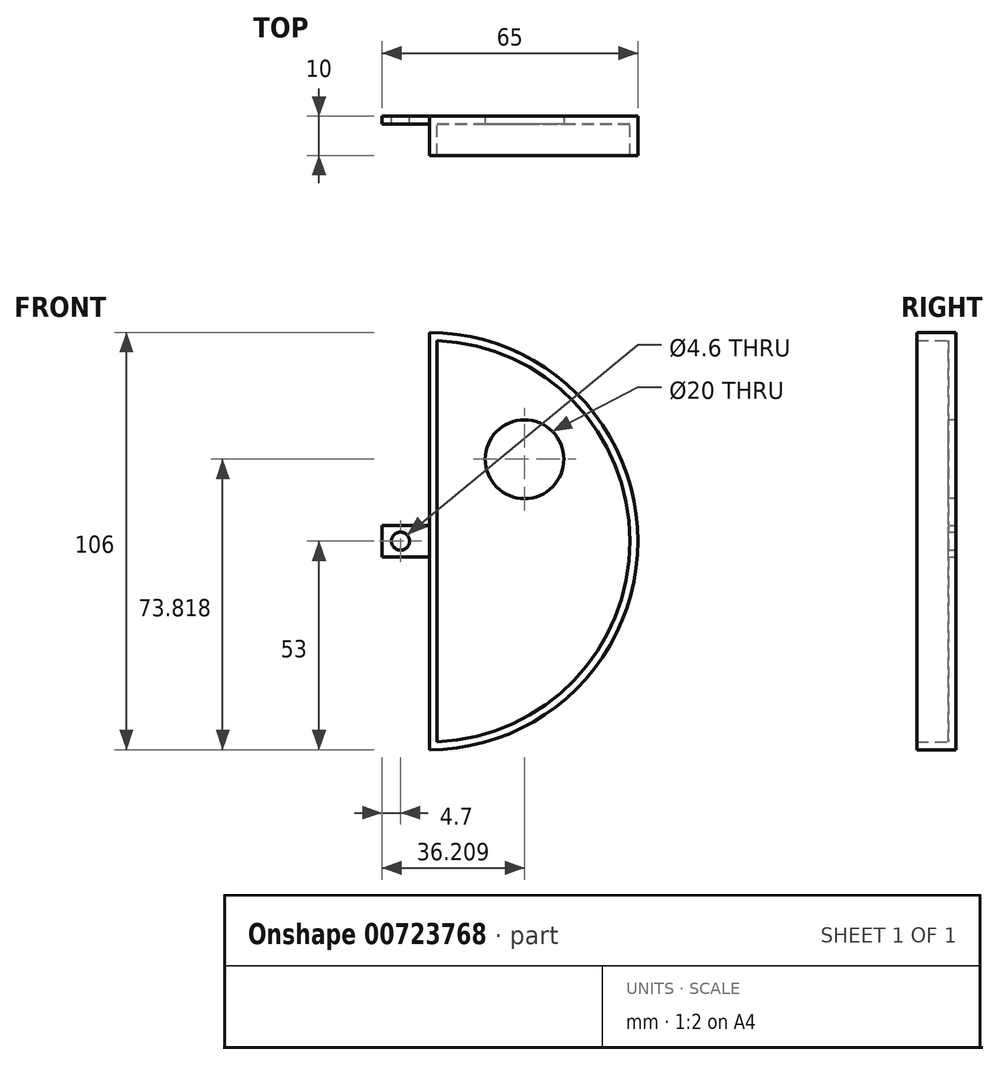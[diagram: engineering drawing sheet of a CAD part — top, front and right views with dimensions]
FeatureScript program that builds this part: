
annotation { "Feature Type Name" : "Feature", "Feature Type Description" : "" }
export const myFeature = defineFeature(function(context is Context, id is Id, definition is map)
    precondition{}
    {
        {
            var Q0;
            Q0=qCreatedBy(makeId("Front.planeOp"),FACE);
            var sketch = newSketch(context, id + "F0", { "sketchPlane" : qUnion([Q0])});
            skArc(sketch, "E0", {"start": v(0, -53) * mm, "mid": v(53, 0) * mm, "end": v(0, 53) * mm});
            skLineSegment(sketch, "E1", {"start": v(0, 53) * mm, "end": v(0, -53) * mm});
            skSolve(sketch);
        }
        {
            var Q0;
            Q0 = qSketchRegion(id + "F0", true);
            extrude(context, id + "F1", {"entities" : qUnion([Q0]), "depth" : 10 * mm, "offsetDistance" : 25 * mm});
        }
        {
            var Q0;
            Q0=makeQuery(id+"F1.opExtrude","CAP_FACE",FACE,{"disambiguationData":[OSD([sQuery(id+"F0.wireOp",EDGE,"E0"),sQuery(id+"F0.wireOp",EDGE,"E1")])],"isStart":false});
            shell(context, id + "F2", {"entities" : qUnion([Q0]), "thickness" : 2 * mm});
        }
        {
            var Q0;
            Q0=qCreatedBy(makeId("Front.planeOp"),FACE);
            var sketch = newSketch(context, id + "F3", { "sketchPlane" : qUnion([Q0])});
            skLineSegment(sketch, "E2.bottom", {"start": v(0, -4) * mm, "end": v(-12, -4) * mm});
            skLineSegment(sketch, "E2.top", {"start": v(0, 4) * mm, "end": v(-12, 4) * mm});
            skLineSegment(sketch, "E2.left", {"start": v(0, -4) * mm, "end": v(0, 4) * mm});
            skLineSegment(sketch, "E2.right", {"start": v(-12, -4) * mm, "end": v(-12, 4) * mm});
            skSolve(sketch);
        }
        {
            var Q0;
            Q0 = qSketchRegion(id + "F3", true);
            extrude(context, id + "F4", {"entities" : qUnion([Q0]), "operationType" : NewBodyOperationType.ADD, "depth" : 2 * mm, "offsetDistance" : 25 * mm});
        }
        {
            var Q0;
            Q0=makeQuery(id+"F4.boolean.opBoolean","MERGE",FACE,{"derivedFrom":[makeQuery(id+"F1.opExtrude","CAP_FACE",FACE,{"disambiguationData":[OSD([sQuery(id+"F0.wireOp",EDGE,"E0"),sQuery(id+"F0.wireOp",EDGE,"E1")])],"isStart":true}),makeQuery(id+"F4.opExtrude","CAP_FACE",FACE,{"disambiguationData":[OSD([sQuery(id+"F3.wireOp",EDGE,"E2.bottom"),sQuery(id+"F3.wireOp",EDGE,"E2.top"),sQuery(id+"F3.wireOp",EDGE,"E2.left"),sQuery(id+"F3.wireOp",EDGE,"E2.right")])],"isStart":true})]});
            var sketch = newSketch(context, id + "F5", { "sketchPlane" : qUnion([Q0])});
            skCircle(sketch, "E3", {"center": v(7.3, 0) * mm, "radius": 2.3 * mm});
            skSolve(sketch);
        }
        {
            var Q0;
            Q0 = qSketchRegion(id + "F5", true);
            extrude(context, id + "F6", {"entities" : qUnion([Q0]), "operationType" : NewBodyOperationType.REMOVE, "oppositeDirection" : true, "depth" : 3 * mm, "offsetDistance" : 25 * mm});
        }
        {
            var Q0;
            Q0=makeQuery(id+"F2.opShell","OFFSET_FACE",FACE,{"disambiguationData":[OSD([sQuery(id+"F0.wireOp",EDGE,"E0"),sQuery(id+"F0.wireOp",EDGE,"E1")])]});
            var sketch = newSketch(context, id + "F7", { "sketchPlane" : qUnion([Q0])});
            skCircle(sketch, "E4", {"center": v(24.2, 20.82) * mm, "radius": 10 * mm});
            skSolve(sketch);
        }
        {
            var Q0;
            Q0=makeQuery(id+"F7.imprint","IMPRINT",FACE,{"disambiguationData":[TD([[makeQuery(id+"F7.imprint","IMPRINT",EDGE,{"derivedFrom":sQuery(id+"F7.wireOp",EDGE,"E4")}),1.0]])]});
            extrude(context, id + "F8", {"entities" : qUnion([Q0]), "operationType" : NewBodyOperationType.REMOVE, "oppositeDirection" : true, "depth" : 25 * mm, "offsetDistance" : 25 * mm});
        }
    });
